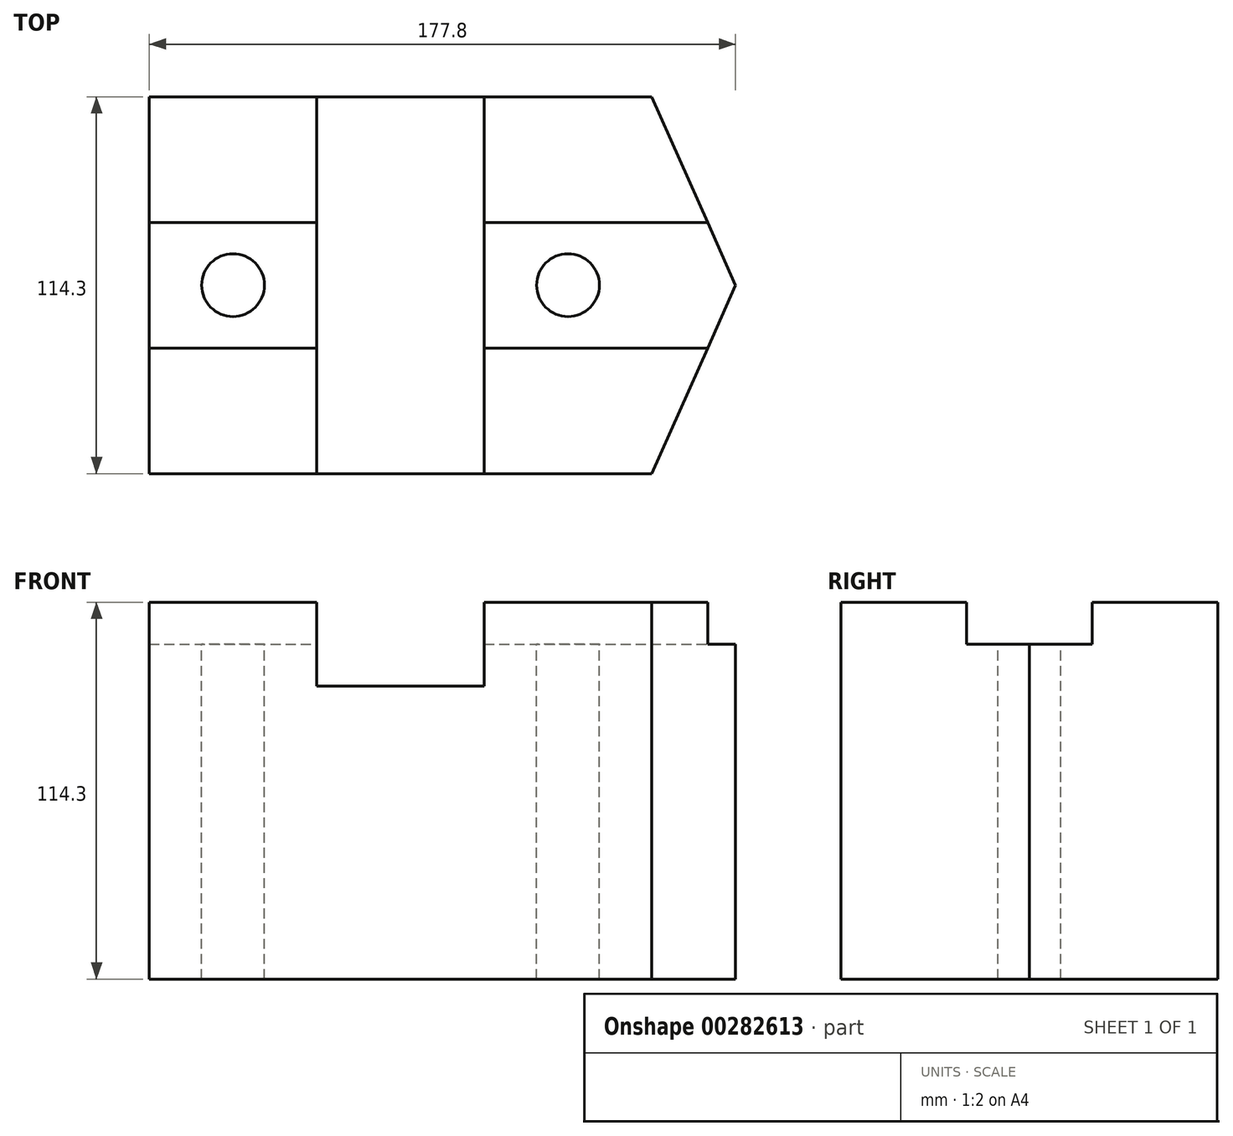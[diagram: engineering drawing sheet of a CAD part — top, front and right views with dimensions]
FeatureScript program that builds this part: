
annotation { "Feature Type Name" : "Feature", "Feature Type Description" : "" }
export const myFeature = defineFeature(function(context is Context, id is Id, definition is map)
    precondition{}
    {
        {
            var Q0;
            Q0=qCreatedBy(makeId("Top.planeOp"),FACE);
            var sketch = newSketch(context, id + "F0", { "sketchPlane" : qUnion([Q0])});
            skLineSegment(sketch, "E0", {"start": v(0, 114.3) * mm, "end": v(0, 0) * mm});
            skLineSegment(sketch, "E1", {"start": v(0, 0) * mm, "end": v(152.4, 0) * mm});
            skLineSegment(sketch, "E2", {"start": v(0, 114.3) * mm, "end": v(152.4, 114.3) * mm});
            skPoint(sketch, "E3", {"position": v(0, 114.3) * mm});
            skPoint(sketch, "E4", {"position": v(50.8, 114.3) * mm});
            skPoint(sketch, "E5", {"position": v(101.6, 114.3) * mm});
            skLineSegment(sketch, "E6", {"start": v(50.8, 114.3) * mm, "end": v(50.8, 0) * mm});
            skLineSegment(sketch, "E7", {"start": v(101.6, 114.3) * mm, "end": v(101.6, 0) * mm});
            skPoint(sketch, "E8", {"position": v(0, 76.2) * mm});
            skPoint(sketch, "E9", {"position": v(0, 38.1) * mm});
            skLineSegment(sketch, "E10", {"start": v(0, 76.2) * mm, "end": v(50.8, 76.2) * mm});
            skLineSegment(sketch, "E11", {"start": v(0, 38.1) * mm, "end": v(50.8, 38.1) * mm});
            skLineSegment(sketch, "E12", {"start": v(0, 57.15) * mm, "end": v(50.8, 57.15) * mm, "construction": true});
            skLineSegment(sketch, "E13", {"start": v(25.4, 76.2) * mm, "end": v(25.4, 38.1) * mm, "construction": true});
            skCircle(sketch, "E14", {"center": v(25.4, 57.15) * mm, "radius": 9.53 * mm});
            skLineSegment(sketch, "E15", {"start": v(127, 76.2) * mm, "end": v(127, 38.1) * mm, "construction": true});
            skCircle(sketch, "E16", {"center": v(127, 57.15) * mm, "radius": 9.53 * mm});
            skLineSegment(sketch, "E17", {"start": v(0, 57.15) * mm, "end": v(177.8, 57.15) * mm, "construction": true});
            skLineSegment(sketch, "E18", {"start": v(152.4, 114.3) * mm, "end": v(177.8, 57.15) * mm});
            skLineSegment(sketch, "E19", {"start": v(177.8, 57.15) * mm, "end": v(152.4, 0) * mm});
            skLineSegment(sketch, "E20", {"start": v(101.6, 38.1) * mm, "end": v(169.33, 38.1) * mm});
            skLineSegment(sketch, "E21", {"start": v(101.6, 76.2) * mm, "end": v(169.33, 76.2) * mm});
            skSolve(sketch);
        }
        {
            var Q0;
            {var subQ3=sQuery(id+"F0.wireOp",EDGE,"E10");Q0=makeQuery(id+"F0.imprint","IMPRINT",FACE,{"disambiguationData":[TD([[makeQuery(id+"F0.imprint","IMPRINT",EDGE,{"derivedFrom":subQ3}),1.0]])]});}
            var Q1;
            {var subQ0=sQuery(id+"F0.wireOp",EDGE,"E10");Q1=makeQuery(id+"F0.imprint","IMPRINT",FACE,{"disambiguationData":[TD([[makeQuery(id+"F0.imprint","IMPRINT",EDGE,{"derivedFrom":subQ0}),-1.0]])]});}
            var Q2;
            {var subQ3=sQuery(id+"F0.wireOp",EDGE,"E11");Q2=makeQuery(id+"F0.imprint","IMPRINT",FACE,{"disambiguationData":[TD([[makeQuery(id+"F0.imprint","IMPRINT",EDGE,{"derivedFrom":subQ3}),-1.0]])]});}
            var Q3;
            {var subQ0=sQuery(id+"F0.wireOp",EDGE,"E6");var subQ7=sQuery(id+"F0.wireOp",EDGE,"E1");var subQ8=makeQuery(id+"F0.imprint","INTERSECT",VERTEX,{"derivedFrom":[subQ7,subQ0]});Q3=makeQuery(id+"F0.imprint","IMPRINT",FACE,{"disambiguationData":[TD([[makeQuery(id+"F0.imprint","IMPRINT",EDGE,{"disambiguationData":[TD([[subQ8,-1.0]])],"derivedFrom":subQ7}),1.0]])]});}
            var Q4;
            {var subQ5=sQuery(id+"F0.wireOp",EDGE,"E21");Q4=makeQuery(id+"F0.imprint","IMPRINT",FACE,{"disambiguationData":[TD([[makeQuery(id+"F0.imprint","IMPRINT",EDGE,{"derivedFrom":subQ5}),1.0]])]});}
            var Q5;
            Q5=makeQuery(id+"F0.imprint","IMPRINT",FACE,{"disambiguationData":[TD([[makeQuery(id+"F0.imprint","IMPRINT",EDGE,{"derivedFrom":sQuery(id+"F0.wireOp",EDGE,"E16")}),-1.0]])]});
            var Q6;
            {var subQ5=sQuery(id+"F0.wireOp",EDGE,"E20");Q6=makeQuery(id+"F0.imprint","IMPRINT",FACE,{"disambiguationData":[TD([[makeQuery(id+"F0.imprint","IMPRINT",EDGE,{"derivedFrom":subQ5}),-1.0]])]});}
            extrude(context, id + "F1", {"entities" : qUnion([Q0, Q1, Q2, Q3, Q4, Q5, Q6]), "oppositeDirection" : true, "depth" : 88.9 * mm});
        }
        {
            var Q0;
            {var subQ3=sQuery(id+"F0.wireOp",EDGE,"E10");Q0=makeQuery(id+"F0.imprint","IMPRINT",FACE,{"disambiguationData":[TD([[makeQuery(id+"F0.imprint","IMPRINT",EDGE,{"derivedFrom":subQ3}),1.0]])]});}
            var Q1;
            {var subQ3=sQuery(id+"F0.wireOp",EDGE,"E11");Q1=makeQuery(id+"F0.imprint","IMPRINT",FACE,{"disambiguationData":[TD([[makeQuery(id+"F0.imprint","IMPRINT",EDGE,{"derivedFrom":subQ3}),-1.0]])]});}
            var Q2;
            {var subQ5=sQuery(id+"F0.wireOp",EDGE,"E21");Q2=makeQuery(id+"F0.imprint","IMPRINT",FACE,{"disambiguationData":[TD([[makeQuery(id+"F0.imprint","IMPRINT",EDGE,{"derivedFrom":subQ5}),1.0]])]});}
            var Q3;
            {var subQ5=sQuery(id+"F0.wireOp",EDGE,"E20");Q3=makeQuery(id+"F0.imprint","IMPRINT",FACE,{"disambiguationData":[TD([[makeQuery(id+"F0.imprint","IMPRINT",EDGE,{"derivedFrom":subQ5}),-1.0]])]});}
            extrude(context, id + "F2", {"entities" : qUnion([Q0, Q1, Q2, Q3]), "operationType" : NewBodyOperationType.ADD, "depth" : 25.4 * mm});
        }
        {
            var Q0;
            {var subQ0=sQuery(id+"F0.wireOp",EDGE,"E10");Q0=makeQuery(id+"F0.imprint","IMPRINT",FACE,{"disambiguationData":[TD([[makeQuery(id+"F0.imprint","IMPRINT",EDGE,{"derivedFrom":subQ0}),-1.0]])]});}
            var Q1;
            Q1=makeQuery(id+"F0.imprint","IMPRINT",FACE,{"disambiguationData":[TD([[makeQuery(id+"F0.imprint","IMPRINT",EDGE,{"derivedFrom":sQuery(id+"F0.wireOp",EDGE,"E16")}),-1.0]])]});
            extrude(context, id + "F3", {"entities" : qUnion([Q0, Q1]), "operationType" : NewBodyOperationType.ADD, "depth" : 12.7 * mm});
        }
    });
